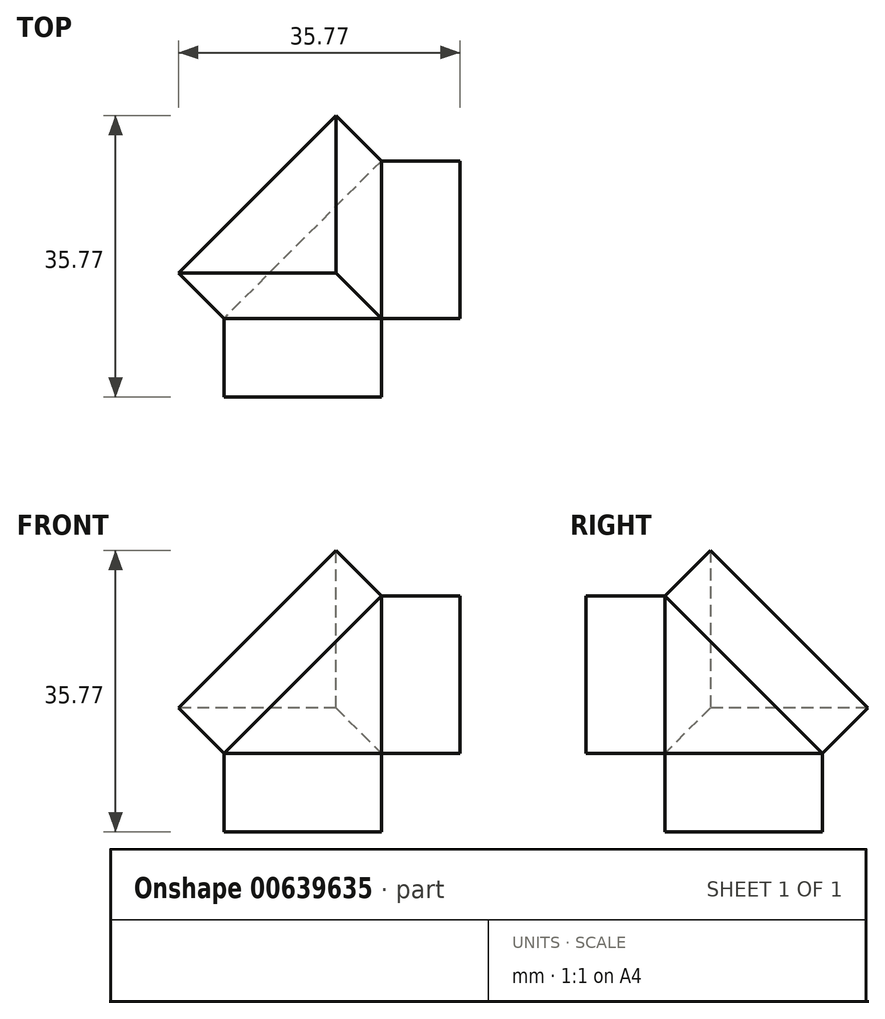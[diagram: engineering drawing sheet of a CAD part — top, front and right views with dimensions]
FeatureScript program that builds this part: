
annotation { "Feature Type Name" : "Feature", "Feature Type Description" : "" }
export const myFeature = defineFeature(function(context is Context, id is Id, definition is map)
    precondition{}
    {
        {
            var Q0;
            Q0=qCreatedBy(makeId("Top.planeOp"),FACE);
            var sketch = newSketch(context, id + "F0", { "sketchPlane" : qUnion([Q0])});
            skLineSegment(sketch, "E0.bottom", {"start": v(10, 10) * mm, "end": v(-10, 10) * mm});
            skLineSegment(sketch, "E0.top", {"start": v(10, -10) * mm, "end": v(-10, -10) * mm});
            skLineSegment(sketch, "E0.left", {"start": v(10, 10) * mm, "end": v(10, -10) * mm});
            skLineSegment(sketch, "E0.right", {"start": v(-10, 10) * mm, "end": v(-10, -10) * mm});
            skPoint(sketch, "E0.middle", {"position": v(0, 0) * mm});
            skSolve(sketch);
        }
        {
            var Q0;
            Q0=makeQuery(id+"F0.imprint","IMPRINT",FACE,{"disambiguationData":[TD([[makeQuery(id+"F0.imprint","IMPRINT",EDGE,{"derivedFrom":sQuery(id+"F0.wireOp",EDGE,"E0.bottom")}),1.0]])]});
            extrude(context, id + "F1", {"entities" : qUnion([Q0]), "depth" : 20 * mm});
        }
        {
            var Q0;
            Q0=makeQuery(id+"F1.opExtrude","SWEPT_EDGE",EDGE,{"disambiguationData":[OSD([sQuery(id+"F0.wireOp",EDGE,"E0.bottom"),sQuery(id+"F0.wireOp",EDGE,"E0.right")])]});
            var Q1;
            Q1=makeQuery(id+"F1.opExtrude","CAP_EDGE",EDGE,{"disambiguationData":[OSD([sQuery(id+"F0.wireOp",EDGE,"E0.right")])],"isStart":false});
            var Q2;
            Q2=makeQuery(id+"F1.opExtrude","CAP_EDGE",EDGE,{"disambiguationData":[OSD([sQuery(id+"F0.wireOp",EDGE,"E0.bottom")])],"isStart":false});
            chamfer(context, id + "F2", {"entities" : qUnion([Q0, Q1, Q2]), "width" : 20 * mm, "tangentPropagation" : true});
        }
        {
            var Q0;
            Q0=makeQuery(id+"F1.opExtrude","SWEPT_FACE",FACE,{"disambiguationData":[OSD([sQuery(id+"F0.wireOp",EDGE,"E0.left")])]});
            var sketch = newSketch(context, id + "F3", { "sketchPlane" : qUnion([Q0])});
            skSolve(sketch);
        }
        {
            var Q0;
            Q0=qSketchRegion(id+"F3",true);
            var Q1;
            {var subQ0=sQuery(id+"F0.wireOp",EDGE,"E0.left");Q1=makeQuery(id+"F3.imprint","IMPRINT",FACE,{"disambiguationData":[TD([[makeQuery(id+"F3.imprint","IMPRINT",EDGE,{"derivedFrom":makeQuery(id+"F1.opExtrude","CAP_EDGE",EDGE,{"disambiguationData":[OSD([subQ0])],"isStart":true})}),-1.0]])]});}
            extrude(context, id + "F4", {"entities" : qUnion([Q0, Q1]), "operationType" : NewBodyOperationType.ADD, "depth" : 10 * mm});
        }
        {
            var Q0;
            {var subQ0=sQuery(id+"F0.wireOp",EDGE,"E0.left");Q0=makeQuery(id+"F4.boolean.opBoolean","MERGE",FACE,{"derivedFrom":[makeQuery(id+"F1.opExtrude","CAP_FACE",FACE,{"disambiguationData":[OSD([sQuery(id+"F0.wireOp",EDGE,"E0.bottom"),sQuery(id+"F0.wireOp",EDGE,"E0.top"),subQ0,sQuery(id+"F0.wireOp",EDGE,"E0.right")])],"isStart":true}),makeQuery(id+"F4.opExtrude","SWEPT_FACE",FACE,{"disambiguationData":[OSD([subQ0])]})]});}
            var sketch = newSketch(context, id + "F5", { "sketchPlane" : qUnion([Q0])});
            skLineSegment(sketch, "E1", {"start": v(10, -10) * mm, "end": v(10, 10) * mm});
            skSolve(sketch);
        }
        {
            var Q0;
            {var subQ0=sQuery(id+"F5.wireOp",EDGE,"E1");Q0=makeQuery(id+"F5.imprint","IMPRINT",FACE,{"disambiguationData":[TD([[makeQuery(id+"F5.imprint","IMPRINT",EDGE,{"derivedFrom":subQ0}),1.0]])]});}
            extrude(context, id + "F6", {"entities" : qUnion([Q0]), "operationType" : NewBodyOperationType.ADD, "depth" : 10 * mm});
        }
        {
            var Q0;
            {var subQ0=sQuery(id+"F0.wireOp",EDGE,"E0.left");var subQ1=sQuery(id+"F0.wireOp",EDGE,"E0.top");Q0=makeQuery(id+"F6.boolean.opBoolean","MERGE",FACE,{"derivedFrom":[makeQuery(id+"F4.boolean.opBoolean","MERGE",FACE,{"derivedFrom":[makeQuery(id+"F1.opExtrude","SWEPT_FACE",FACE,{"disambiguationData":[OSD([subQ1])]}),makeQuery(id+"F4.opExtrude","SWEPT_FACE",FACE,{"disambiguationData":[OSD([subQ1,subQ0])]})]}),makeQuery(id+"F6.opExtrude","SWEPT_FACE",FACE,{"disambiguationData":[OSD([subQ1,subQ0])]})]});}
            var sketch = newSketch(context, id + "F7", { "sketchPlane" : qUnion([Q0])});
            skLineSegment(sketch, "E2", {"start": v(10, 0) * mm, "end": v(-10, 0) * mm});
            skLineSegment(sketch, "E3", {"start": v(10, 0) * mm, "end": v(10, 20) * mm});
            skSolve(sketch);
        }
        {
            var Q0;
            Q0=makeQuery(id+"F7.imprint","IMPRINT",FACE,{"disambiguationData":[TD([[makeQuery(id+"F7.imprint","IMPRINT",EDGE,{"derivedFrom":sQuery(id+"F7.wireOp",EDGE,"E2")}),-1.0]])]});
            extrude(context, id + "F8", {"entities" : qUnion([Q0]), "operationType" : NewBodyOperationType.ADD, "depth" : 10 * mm});
        }
        {
            var Q0;
            Q0=makeQuery(id+"F2.opChamfer","BLEND_FACE",FACE,{"disambiguationData":[OSD([sQuery(id+"F0.wireOp",EDGE,"E0.bottom"),sQuery(id+"F0.wireOp",EDGE,"E0.right")])]});
            extrude(context, id + "F9", {"entities" : qUnion([Q0]), "operationType" : NewBodyOperationType.ADD, "depth" : 10 * mm});
        }
    });
